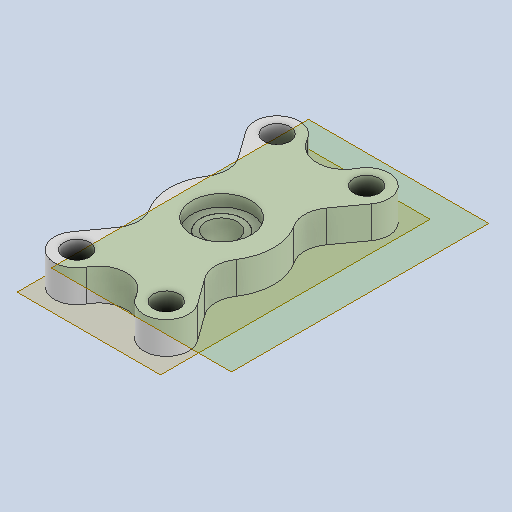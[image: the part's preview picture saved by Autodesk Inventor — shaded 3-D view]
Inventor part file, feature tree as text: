
AUTODESK INVENTOR PART (.ipt)
format: ipt  version: 2022 (Build 260153000, 153)  size: 236,032 bytes
history: native  units: mm
features: reference x6, other x5, plane x4, sketch x3, extrude x3
ambient origin geometry x8: Origin, YZ Plane, XZ Plane, XY Plane, X Axis, Y Axis, Z Axis, Center Point
bodies: Solid1 (feature_tree)
feature tree (21):
  plane  "Work Plane1"
  sketch  "Sketch1"  dims[d1=0.3mm d2=0.3mm]
  plane  "Work Plane2"
  extrude  "Extrusion1"  Depth=0.3mm
  sketch  "Sketch3"  dims[d3=10.0mm d4=0.0mm d8=0.3mm]
  plane  "Work Plane4"
  extrude  "Extrusion3"  Depth=10.0mm
  extrude  "Extrusion4"  Depth=0.1mm
  plane  "Work Plane5"
  reference  "Reference1"
  reference  "Reference2"
  reference  "Reference3"
  reference  "Reference5"
  sketch  "Sketch4"  dims[d9=0.3mm d11=0.3mm d12=10.0mm d13=0.0mm d14=0.1mm d15=0.0mm d20=0.3mm]
  reference  "Reference7"
  reference  "Reference8"
  other  "<userpath>\OneDrive - Imperial College London\ROBOICP MK2\solids feeder assembly.iam"
  other  "solids feeder assembly.iam"
  other  "screw_casing:1"
  other  "smol stepper:1"
  other  "Screw Shaft:1"
